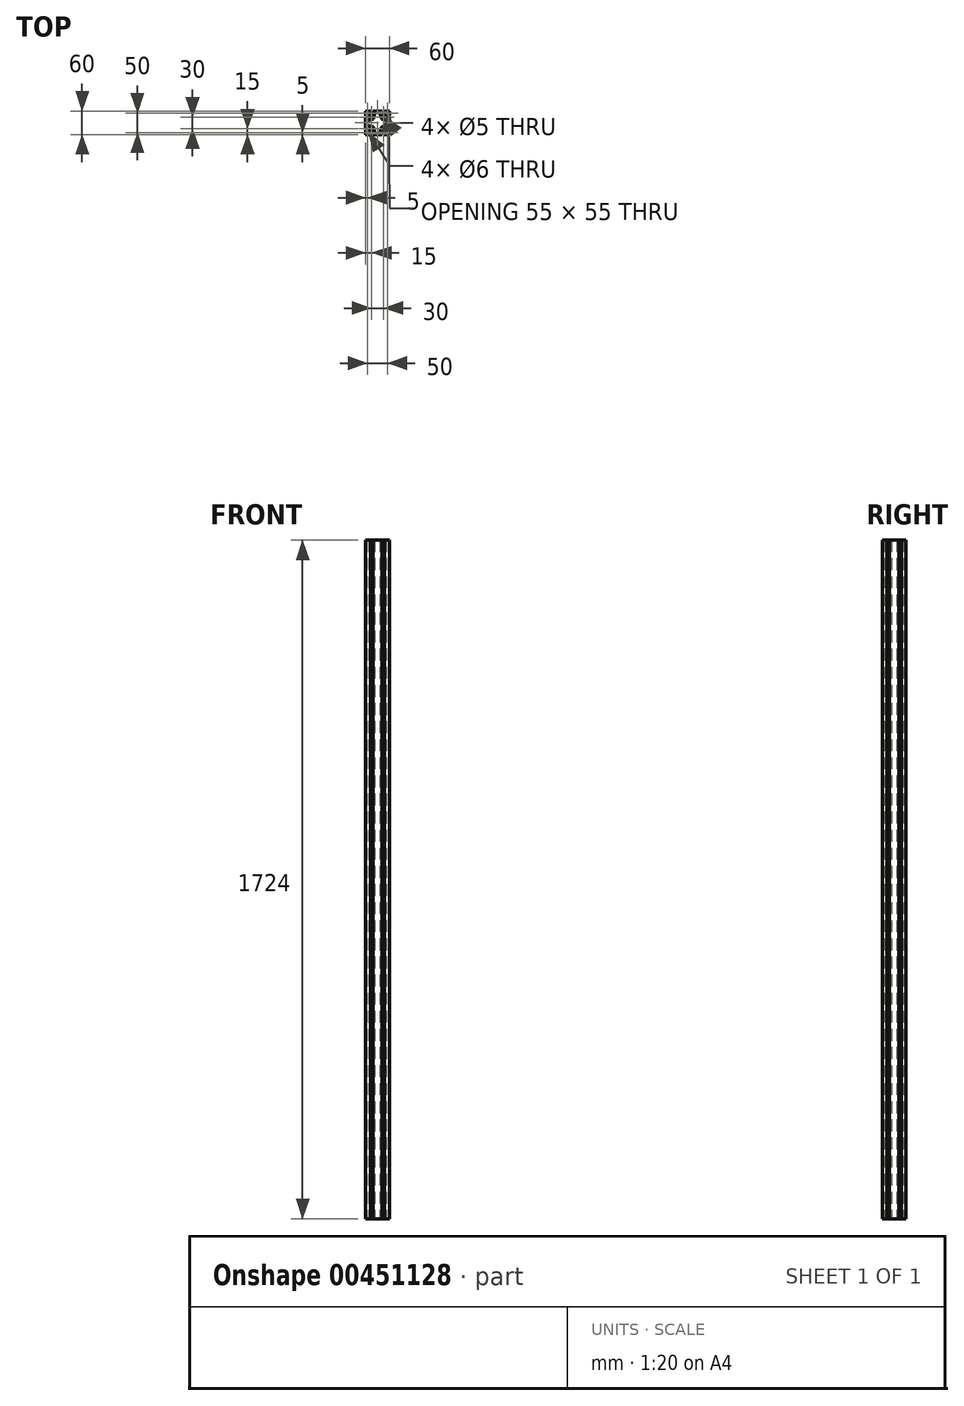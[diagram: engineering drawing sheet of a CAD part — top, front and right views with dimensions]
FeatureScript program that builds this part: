
annotation { "Feature Type Name" : "Feature", "Feature Type Description" : "" }
export const myFeature = defineFeature(function(context is Context, id is Id, definition is map)
    precondition{}
    {
        {
            var Q0;
            Q0=qCreatedBy(makeId("Top.planeOp"),FACE);
            var sketch = newSketch(context, id + "F0", { "sketchPlane" : qUnion([Q0])});
            skLineSegment(sketch, "E0.bottom", {"start": v(30, -30) * mm, "end": v(-30, -30) * mm});
            skLineSegment(sketch, "E0.top", {"start": v(30, 30) * mm, "end": v(-30, 30) * mm});
            skLineSegment(sketch, "E0.left", {"start": v(30, -30) * mm, "end": v(30, 30) * mm});
            skLineSegment(sketch, "E0.right", {"start": v(-30, -30) * mm, "end": v(-30, 30) * mm});
            skPoint(sketch, "E0.middle", {"position": v(0, 0) * mm});
            skLineSegment(sketch, "E1.top", {"start": v(-11.85, 30) * mm, "end": v(-18.15, 30) * mm});
            skLineSegment(sketch, "E1.left", {"start": v(-11.85, 27.5) * mm, "end": v(-11.85, 30) * mm});
            skLineSegment(sketch, "E1.right", {"start": v(-18.15, 27.5) * mm, "end": v(-18.15, 30) * mm});
            skPoint(sketch, "E1.middle", {"position": v(-15, 28.75) * mm});
            skLineSegment(sketch, "E2.bottom", {"start": v(-9.85, 27.5) * mm, "end": v(-11.85, 27.5) * mm});
            skLineSegment(sketch, "E2.left", {"start": v(-9.85, 27.5) * mm, "end": v(-9.85, 21.55) * mm});
            skLineSegment(sketch, "E2.right", {"start": v(-20.15, 27.5) * mm, "end": v(-20.15, 21.55) * mm});
            skPoint(sketch, "E2.middle", {"position": v(-15, 24.52) * mm});
            skArc(sketch, "E3", {"start": v(-20.15, 21.55) * mm, "mid": v(-15, 19.5) * mm, "end": v(-9.85, 21.55) * mm});
            skPoint(sketch, "E4.MirrorP", {"position": v(15, 24.52) * mm});
            skPoint(sketch, "E5.MirrorP", {"position": v(15, 28.75) * mm});
            skLineSegment(sketch, "E6.MirrorCS", {"start": v(11.85, 27.5) * mm, "end": v(11.85, 30) * mm});
            skLineSegment(sketch, "E7.MirrorCS", {"start": v(18.15, 27.5) * mm, "end": v(18.15, 30) * mm});
            skLineSegment(sketch, "E8.MirrorCS", {"start": v(9.85, 27.5) * mm, "end": v(11.85, 27.5) * mm});
            skLineSegment(sketch, "E9.MirrorCS", {"start": v(9.85, 27.5) * mm, "end": v(9.85, 21.55) * mm});
            skArc(sketch, "E10.MirrorCS", {"start": v(20.15, 21.55) * mm, "mid": v(15, 19.5) * mm, "end": v(9.85, 21.55) * mm});
            skLineSegment(sketch, "E11.MirrorCS", {"start": v(20.15, 27.5) * mm, "end": v(20.15, 21.55) * mm});
            skLineSegment(sketch, "E12.MirrorCS", {"start": v(11.85, 30) * mm, "end": v(18.15, 30) * mm});
            skLineSegment(sketch, "E13.1.0", {"start": v(27.5, 20.15) * mm, "end": v(21.55, 20.15) * mm});
            skLineSegment(sketch, "E13.1.1", {"start": v(27.5, 9.85) * mm, "end": v(21.55, 9.85) * mm});
            skArc(sketch, "E13.1.2", {"start": v(21.55, 20.15) * mm, "mid": v(19.5, 15) * mm, "end": v(21.55, 9.85) * mm});
            skLineSegment(sketch, "E13.1.3", {"start": v(27.5, -9.85) * mm, "end": v(21.55, -9.85) * mm});
            skLineSegment(sketch, "E13.1.4", {"start": v(27.5, -20.15) * mm, "end": v(21.55, -20.15) * mm});
            skPoint(sketch, "E13.1.5", {"position": v(28.75, 15) * mm});
            skPoint(sketch, "E13.1.6", {"position": v(28.75, -15) * mm});
            skArc(sketch, "E13.1.7", {"start": v(21.55, -20.15) * mm, "mid": v(19.5, -15) * mm, "end": v(21.55, -9.85) * mm});
            skPoint(sketch, "E13.1.8", {"position": v(24.52, -15) * mm});
            skPoint(sketch, "E13.1.9", {"position": v(24.52, 15) * mm});
            skLineSegment(sketch, "E13.1.10", {"start": v(27.5, 9.85) * mm, "end": v(27.5, 20.15) * mm});
            skLineSegment(sketch, "E13.1.11", {"start": v(27.5, -11.85) * mm, "end": v(27.5, -18.15) * mm});
            skLineSegment(sketch, "E13.1.12", {"start": v(30, 11.85) * mm, "end": v(30, 18.15) * mm});
            skLineSegment(sketch, "E13.1.13", {"start": v(30, -11.85) * mm, "end": v(30, -18.15) * mm});
            skLineSegment(sketch, "E13.1.14", {"start": v(27.5, 18.15) * mm, "end": v(30, 18.15) * mm});
            skLineSegment(sketch, "E13.1.15", {"start": v(27.5, 11.85) * mm, "end": v(30, 11.85) * mm});
            skLineSegment(sketch, "E13.1.16", {"start": v(27.5, 11.85) * mm, "end": v(27.5, 18.15) * mm});
            skLineSegment(sketch, "E13.1.17", {"start": v(27.5, -9.85) * mm, "end": v(27.5, -20.15) * mm});
            skLineSegment(sketch, "E13.1.18", {"start": v(27.5, -18.15) * mm, "end": v(30, -18.15) * mm});
            skLineSegment(sketch, "E13.1.19", {"start": v(27.5, -11.85) * mm, "end": v(30, -11.85) * mm});
            skLineSegment(sketch, "E13.2.0", {"start": v(20.15, -27.5) * mm, "end": v(20.15, -21.55) * mm});
            skLineSegment(sketch, "E13.2.1", {"start": v(9.85, -27.5) * mm, "end": v(9.85, -21.55) * mm});
            skArc(sketch, "E13.2.2", {"start": v(20.15, -21.55) * mm, "mid": v(15, -19.5) * mm, "end": v(9.85, -21.55) * mm});
            skLineSegment(sketch, "E13.2.3", {"start": v(-9.85, -27.5) * mm, "end": v(-9.85, -21.55) * mm});
            skLineSegment(sketch, "E13.2.4", {"start": v(-20.15, -27.5) * mm, "end": v(-20.15, -21.55) * mm});
            skPoint(sketch, "E13.2.5", {"position": v(15, -28.75) * mm});
            skPoint(sketch, "E13.2.6", {"position": v(-15, -28.75) * mm});
            skArc(sketch, "E13.2.7", {"start": v(-20.15, -21.55) * mm, "mid": v(-15, -19.5) * mm, "end": v(-9.85, -21.55) * mm});
            skPoint(sketch, "E13.2.8", {"position": v(-15, -24.52) * mm});
            skPoint(sketch, "E13.2.9", {"position": v(15, -24.52) * mm});
            skLineSegment(sketch, "E13.2.10", {"start": v(9.85, -27.5) * mm, "end": v(20.15, -27.5) * mm});
            skLineSegment(sketch, "E13.2.11", {"start": v(-11.85, -27.5) * mm, "end": v(-18.15, -27.5) * mm});
            skLineSegment(sketch, "E13.2.12", {"start": v(11.85, -30) * mm, "end": v(18.15, -30) * mm});
            skLineSegment(sketch, "E13.2.13", {"start": v(-11.85, -30) * mm, "end": v(-18.15, -30) * mm});
            skLineSegment(sketch, "E13.2.14", {"start": v(18.15, -27.5) * mm, "end": v(18.15, -30) * mm});
            skLineSegment(sketch, "E13.2.15", {"start": v(11.85, -27.5) * mm, "end": v(11.85, -30) * mm});
            skLineSegment(sketch, "E13.2.16", {"start": v(11.85, -27.5) * mm, "end": v(18.15, -27.5) * mm});
            skLineSegment(sketch, "E13.2.17", {"start": v(-9.85, -27.5) * mm, "end": v(-20.15, -27.5) * mm});
            skLineSegment(sketch, "E13.2.18", {"start": v(-18.15, -27.5) * mm, "end": v(-18.15, -30) * mm});
            skLineSegment(sketch, "E13.2.19", {"start": v(-11.85, -27.5) * mm, "end": v(-11.85, -30) * mm});
            skLineSegment(sketch, "E13.3.0", {"start": v(-27.5, -20.15) * mm, "end": v(-21.55, -20.15) * mm});
            skLineSegment(sketch, "E13.3.1", {"start": v(-27.5, -9.85) * mm, "end": v(-21.55, -9.85) * mm});
            skArc(sketch, "E13.3.2", {"start": v(-21.55, -20.15) * mm, "mid": v(-19.5, -15) * mm, "end": v(-21.55, -9.85) * mm});
            skLineSegment(sketch, "E13.3.3", {"start": v(-27.5, 9.85) * mm, "end": v(-21.55, 9.85) * mm});
            skLineSegment(sketch, "E13.3.4", {"start": v(-27.5, 20.15) * mm, "end": v(-21.55, 20.15) * mm});
            skPoint(sketch, "E13.3.5", {"position": v(-28.75, -15) * mm});
            skPoint(sketch, "E13.3.6", {"position": v(-28.75, 15) * mm});
            skArc(sketch, "E13.3.7", {"start": v(-21.55, 20.15) * mm, "mid": v(-19.5, 15) * mm, "end": v(-21.55, 9.85) * mm});
            skPoint(sketch, "E13.3.8", {"position": v(-24.52, 15) * mm});
            skPoint(sketch, "E13.3.9", {"position": v(-24.52, -15) * mm});
            skLineSegment(sketch, "E13.3.10", {"start": v(-27.5, -9.85) * mm, "end": v(-27.5, -20.15) * mm});
            skLineSegment(sketch, "E13.3.11", {"start": v(-27.5, 11.85) * mm, "end": v(-27.5, 18.15) * mm});
            skLineSegment(sketch, "E13.3.12", {"start": v(-30, -11.85) * mm, "end": v(-30, -18.15) * mm});
            skLineSegment(sketch, "E13.3.13", {"start": v(-30, 11.85) * mm, "end": v(-30, 18.15) * mm});
            skLineSegment(sketch, "E13.3.14", {"start": v(-27.5, -18.15) * mm, "end": v(-30, -18.15) * mm});
            skLineSegment(sketch, "E13.3.15", {"start": v(-27.5, -11.85) * mm, "end": v(-30, -11.85) * mm});
            skLineSegment(sketch, "E13.3.16", {"start": v(-27.5, -11.85) * mm, "end": v(-27.5, -18.15) * mm});
            skLineSegment(sketch, "E13.3.17", {"start": v(-27.5, 9.85) * mm, "end": v(-27.5, 20.15) * mm});
            skLineSegment(sketch, "E13.3.18", {"start": v(-27.5, 18.15) * mm, "end": v(-30, 18.15) * mm});
            skLineSegment(sketch, "E13.3.19", {"start": v(-27.5, 11.85) * mm, "end": v(-30, 11.85) * mm});
            skLineSegment(sketch, "E13.anchor1", {"start": v(0, 0) * mm, "end": v(-20.15, 21.55) * mm, "construction": true});
            skLineSegment(sketch, "E13.anchor2", {"start": v(0, 0) * mm, "end": v(-21.55, -20.15) * mm, "construction": true});
            skLineSegment(sketch, "E14.trimOffspring", {"start": v(-18.15, 27.5) * mm, "end": v(-20.15, 27.5) * mm});
            skLineSegment(sketch, "E15.trimOffspring", {"start": v(18.15, 27.5) * mm, "end": v(20.15, 27.5) * mm});
            skCircle(sketch, "E16", {"center": v(-15, 15) * mm, "radius": 2.5 * mm});
            skCircle(sketch, "E17", {"center": v(-25, 25) * mm, "radius": 3 * mm});
            skCircle(sketch, "E18.MirrorC", {"center": v(25, 25) * mm, "radius": 3 * mm});
            skCircle(sketch, "E19.MirrorC", {"center": v(25, -25) * mm, "radius": 3 * mm});
            skCircle(sketch, "E20.MirrorC", {"center": v(-25, -25) * mm, "radius": 3 * mm});
            skCircle(sketch, "E21.MirrorC", {"center": v(15, 15) * mm, "radius": 2.5 * mm});
            skCircle(sketch, "E22.MirrorC", {"center": v(15, -15) * mm, "radius": 2.5 * mm});
            skCircle(sketch, "E23.MirrorC", {"center": v(-15, -15) * mm, "radius": 2.5 * mm});
            skLineSegment(sketch, "E24", {"start": v(-7, 27.5) * mm, "end": v(0, 27.5) * mm});
            skLineSegment(sketch, "E25", {"start": v(-7, 27.5) * mm, "end": v(-7, 22) * mm});
            skLineSegment(sketch, "E26", {"start": v(-10, 10) * mm, "end": v(-10, 16) * mm});
            skLineSegment(sketch, "E27", {"start": v(-10, 16) * mm, "end": v(-7, 22) * mm});
            skLineSegment(sketch, "E28.MirrorCS", {"start": v(10, 10) * mm, "end": v(10, 16) * mm});
            skLineSegment(sketch, "E29.MirrorCS", {"start": v(10, 16) * mm, "end": v(7, 22) * mm});
            skLineSegment(sketch, "E30.MirrorCS", {"start": v(7, 27.5) * mm, "end": v(0, 27.5) * mm});
            skLineSegment(sketch, "E31.MirrorCS", {"start": v(7, 27.5) * mm, "end": v(7, 22) * mm});
            skLineSegment(sketch, "E32.1.0", {"start": v(-10, -10) * mm, "end": v(-16, -10) * mm});
            skLineSegment(sketch, "E32.1.1", {"start": v(-16, -10) * mm, "end": v(-22, -7) * mm});
            skLineSegment(sketch, "E32.1.2", {"start": v(-27.5, -7) * mm, "end": v(-22, -7) * mm});
            skLineSegment(sketch, "E32.1.3", {"start": v(-27.5, -7) * mm, "end": v(-27.5, 0) * mm});
            skLineSegment(sketch, "E32.1.4", {"start": v(-27.5, 7) * mm, "end": v(-27.5, 0) * mm});
            skLineSegment(sketch, "E32.1.5", {"start": v(-27.5, 7) * mm, "end": v(-22, 7) * mm});
            skLineSegment(sketch, "E32.1.6", {"start": v(-16, 10) * mm, "end": v(-22, 7) * mm});
            skLineSegment(sketch, "E32.1.7", {"start": v(-10, 10) * mm, "end": v(-16, 10) * mm});
            skLineSegment(sketch, "E32.2.0", {"start": v(10, -10) * mm, "end": v(10, -16) * mm});
            skLineSegment(sketch, "E32.2.1", {"start": v(10, -16) * mm, "end": v(7, -22) * mm});
            skLineSegment(sketch, "E32.2.2", {"start": v(7, -27.5) * mm, "end": v(7, -22) * mm});
            skLineSegment(sketch, "E32.2.3", {"start": v(7, -27.5) * mm, "end": v(0, -27.5) * mm});
            skLineSegment(sketch, "E32.2.4", {"start": v(-7, -27.5) * mm, "end": v(0, -27.5) * mm});
            skLineSegment(sketch, "E32.2.5", {"start": v(-7, -27.5) * mm, "end": v(-7, -22) * mm});
            skLineSegment(sketch, "E32.2.6", {"start": v(-10, -16) * mm, "end": v(-7, -22) * mm});
            skLineSegment(sketch, "E32.2.7", {"start": v(-10, -10) * mm, "end": v(-10, -16) * mm});
            skLineSegment(sketch, "E32.3.0", {"start": v(10, 10) * mm, "end": v(16, 10) * mm});
            skLineSegment(sketch, "E32.3.1", {"start": v(16, 10) * mm, "end": v(22, 7) * mm});
            skLineSegment(sketch, "E32.3.2", {"start": v(27.5, 7) * mm, "end": v(22, 7) * mm});
            skLineSegment(sketch, "E32.3.3", {"start": v(27.5, 7) * mm, "end": v(27.5, 0) * mm});
            skLineSegment(sketch, "E32.3.4", {"start": v(27.5, -7) * mm, "end": v(27.5, 0) * mm});
            skLineSegment(sketch, "E32.3.5", {"start": v(27.5, -7) * mm, "end": v(22, -7) * mm});
            skLineSegment(sketch, "E32.3.6", {"start": v(16, -10) * mm, "end": v(22, -7) * mm});
            skLineSegment(sketch, "E32.3.7", {"start": v(10, -10) * mm, "end": v(16, -10) * mm});
            skSolve(sketch);
        }
        {
            var Q0;
            {var subQ30=sQuery(id+"F0.wireOp",EDGE,"E1.left");Q0=makeQuery(id+"F0.imprint","IMPRINT",FACE,{"disambiguationData":[TD([[makeQuery(id+"F0.imprint","IMPRINT",EDGE,{"derivedFrom":subQ30}),-1.0]])]});}
            extrude(context, id + "F1", {"entities" : qUnion([Q0]), "offsetDistance" : 25 * mm, "depth" : 1724 * mm});
        }
        {
            var Q0;
            Q0=makeQuery(id+"F1.opExtrude","SWEPT_EDGE",EDGE,{"disambiguationData":[OSD([sQuery(id+"F0.wireOp",EDGE,"E24"),sQuery(id+"F0.wireOp",EDGE,"E25")])]});
            var Q1;
            Q1=makeQuery(id+"F1.opExtrude","SWEPT_EDGE",EDGE,{"disambiguationData":[OSD([sQuery(id+"F0.wireOp",EDGE,"E30.MirrorCS"),sQuery(id+"F0.wireOp",EDGE,"E31.MirrorCS")])]});
            var Q2;
            Q2=makeQuery(id+"F1.opExtrude","SWEPT_EDGE",EDGE,{"disambiguationData":[OSD([sQuery(id+"F0.wireOp",EDGE,"840db5bc-c403-45cd-90c7-254e62d9e8c5.3.2"),sQuery(id+"F0.wireOp",EDGE,"840db5bc-c403-45cd-90c7-254e62d9e8c5.3.3")])]});
            var Q3;
            Q3=makeQuery(id+"F1.opExtrude","SWEPT_EDGE",EDGE,{"disambiguationData":[OSD([sQuery(id+"F0.wireOp",EDGE,"840db5bc-c403-45cd-90c7-254e62d9e8c5.3.4"),sQuery(id+"F0.wireOp",EDGE,"840db5bc-c403-45cd-90c7-254e62d9e8c5.3.5")])]});
            var Q4;
            Q4=makeQuery(id+"F1.opExtrude","SWEPT_EDGE",EDGE,{"disambiguationData":[OSD([sQuery(id+"F0.wireOp",EDGE,"840db5bc-c403-45cd-90c7-254e62d9e8c5.1.4"),sQuery(id+"F0.wireOp",EDGE,"840db5bc-c403-45cd-90c7-254e62d9e8c5.1.5")])]});
            var Q5;
            Q5=makeQuery(id+"F1.opExtrude","SWEPT_EDGE",EDGE,{"disambiguationData":[OSD([sQuery(id+"F0.wireOp",EDGE,"840db5bc-c403-45cd-90c7-254e62d9e8c5.1.2"),sQuery(id+"F0.wireOp",EDGE,"840db5bc-c403-45cd-90c7-254e62d9e8c5.1.3")])]});
            var Q6;
            Q6=makeQuery(id+"F1.opExtrude","SWEPT_EDGE",EDGE,{"disambiguationData":[OSD([sQuery(id+"F0.wireOp",EDGE,"840db5bc-c403-45cd-90c7-254e62d9e8c5.2.2"),sQuery(id+"F0.wireOp",EDGE,"840db5bc-c403-45cd-90c7-254e62d9e8c5.2.3")])]});
            var Q7;
            Q7=makeQuery(id+"F1.opExtrude","SWEPT_EDGE",EDGE,{"disambiguationData":[OSD([sQuery(id+"F0.wireOp",EDGE,"840db5bc-c403-45cd-90c7-254e62d9e8c5.2.4"),sQuery(id+"F0.wireOp",EDGE,"840db5bc-c403-45cd-90c7-254e62d9e8c5.2.5")])]});
            fillet(context, id + "F2", {"entities" : qUnion([Q0, Q1, Q2, Q3, Q4, Q5, Q6, Q7]), "radius" : 2 * mm, "tangentPropagation" : true, "allowEdgeOverflow" : false});
        }
        {
            var Q0;
            Q0=makeQuery(id+"F1.opExtrude","SWEPT_EDGE",EDGE,{"disambiguationData":[OSD([sQuery(id+"F0.wireOp",EDGE,"E26"),sQuery(id+"F0.wireOp",EDGE,"E27")])]});
            var Q1;
            Q1=makeQuery(id+"F1.opExtrude","SWEPT_EDGE",EDGE,{"disambiguationData":[OSD([sQuery(id+"F0.wireOp",EDGE,"E28.MirrorCS"),sQuery(id+"F0.wireOp",EDGE,"E29.MirrorCS")])]});
            var Q2;
            Q2=makeQuery(id+"F1.opExtrude","SWEPT_EDGE",EDGE,{"disambiguationData":[OSD([sQuery(id+"F0.wireOp",EDGE,"840db5bc-c403-45cd-90c7-254e62d9e8c5.3.0"),sQuery(id+"F0.wireOp",EDGE,"840db5bc-c403-45cd-90c7-254e62d9e8c5.3.1")])]});
            var Q3;
            Q3=makeQuery(id+"F1.opExtrude","SWEPT_EDGE",EDGE,{"disambiguationData":[OSD([sQuery(id+"F0.wireOp",EDGE,"840db5bc-c403-45cd-90c7-254e62d9e8c5.1.6"),sQuery(id+"F0.wireOp",EDGE,"840db5bc-c403-45cd-90c7-254e62d9e8c5.1.7")])]});
            var Q4;
            Q4=makeQuery(id+"F1.opExtrude","SWEPT_EDGE",EDGE,{"disambiguationData":[OSD([sQuery(id+"F0.wireOp",EDGE,"840db5bc-c403-45cd-90c7-254e62d9e8c5.1.0"),sQuery(id+"F0.wireOp",EDGE,"840db5bc-c403-45cd-90c7-254e62d9e8c5.1.1")])]});
            var Q5;
            Q5=makeQuery(id+"F1.opExtrude","SWEPT_EDGE",EDGE,{"disambiguationData":[OSD([sQuery(id+"F0.wireOp",EDGE,"840db5bc-c403-45cd-90c7-254e62d9e8c5.3.6"),sQuery(id+"F0.wireOp",EDGE,"840db5bc-c403-45cd-90c7-254e62d9e8c5.3.7")])]});
            var Q6;
            Q6=makeQuery(id+"F1.opExtrude","SWEPT_EDGE",EDGE,{"disambiguationData":[OSD([sQuery(id+"F0.wireOp",EDGE,"840db5bc-c403-45cd-90c7-254e62d9e8c5.2.0"),sQuery(id+"F0.wireOp",EDGE,"840db5bc-c403-45cd-90c7-254e62d9e8c5.2.1")])]});
            var Q7;
            Q7=makeQuery(id+"F1.opExtrude","SWEPT_EDGE",EDGE,{"disambiguationData":[OSD([sQuery(id+"F0.wireOp",EDGE,"840db5bc-c403-45cd-90c7-254e62d9e8c5.2.6"),sQuery(id+"F0.wireOp",EDGE,"840db5bc-c403-45cd-90c7-254e62d9e8c5.2.7")])]});
            fillet(context, id + "F3", {"entities" : qUnion([Q0, Q1, Q2, Q3, Q4, Q5, Q6, Q7]), "radius" : 7 * mm, "tangentPropagation" : true, "allowEdgeOverflow" : false});
        }
    });
